# Revit family: RN 90033 Optifitt-Serra-Verlängerung
name_source: partatom
category: Rohrformteile
units: mm (PartAtom-declared; Revit-internal decimal feet)

## family parameters
Arbeitsebenenbasiert = Nein
Beim Laden mit Abzugskörper schneiden = Nein
Bemaßung runder Anschluss = Durchmesser verwenden
Gemeinsam genutzt = Nein
Immer vertikal = Ja
Teiletyp = Nicht definiert

## types (15) — shared parameters
1.010.00.2 Blattnummer der Richtlinie = 29
1.010.00.3 Ausgabedatum (Monat) der Richtlinie = 201308
1.010.00.4 Herstellername = R. Nussbaum AG
1.010.00.5 Revisionsdatum der Datei = 20190521
1.010.00.6 Webadresse des Herstellers = http://www.nussbaum.ch
1.100.00.4 Produktbezeichnung = Versorgung
1.110.00.2 Index = 3
1.110.00.4 Produktbezeichnung = Optifitt-Serra
1.960/3L.00.8 Link (URL) = https://www.nussbaum.ch
29.700.00.4 Produktname = Optifitt-Serra-Verlängerung
29.700.00.5 Produktkennung = 2
29.700.00.6 Querschnittsform = 1
29.700.00.7 Nennweitensystem = DN
29.700.00.8 Nenndrucksystem = PN
29.710.02.4 Nenndruck = 16
29.710.02.5 max. zul. Überdruck [hPa] = 1600
29.710.02.7 max. zul. Dauer-Betriebsdruck [hPa] = 1600
29.710.02.9 max. zul. Dauer-Betriebstemperatur [°C] = 90
Connector Visibility = Nein
EnclosingSpace Visibility = Nein
R. Nussbaum AG 90033.18 de Visibility = Nein
R. Nussbaum AG 90033.19 de Visibility = Nein
R. Nussbaum AG 90033.23 de Visibility = Nein
R. Nussbaum AG 90033.24 de Visibility = Nein
R. Nussbaum AG 90033.26 de Visibility = Nein
R. Nussbaum AG 90033.27 de Visibility = Nein
R. Nussbaum AG 90033.28 de Visibility = Nein
R. Nussbaum AG 90033.29 de Visibility = Nein
R. Nussbaum AG 90033.35 de Visibility = Nein
R. Nussbaum AG 90033.36 de Visibility = Nein
R. Nussbaum AG 90033.37 de Visibility = Nein
R. Nussbaum AG 90033.40 de Visibility = Nein
R. Nussbaum AG 90033.41 de Visibility = Nein
R. Nussbaum AG 90033.42 de Visibility = Nein

## per-type parameters (varying)
- DN=25: 1.800.00.3 TGA-Nummer=01900300000000000000000000000000000000000000000020000000000000000048; 1.800.00.4 Kommentarfeld=90033.50, Optifitt-Serra-Verlängerung, DN=25, L=25, R=1, Rp=1; 1.810.00.3 Hersteller-Bestellnummer=90033.50; 1.810.00.4 DATANORM-Nummer=90033.50; 1.810.00.6 GTIN-Nummer=7612945034908; 29.710.02.10 Formstück-Gewicht [kg]=0.147; 29.710.02.3 Benennung=Optifitt-Serra-Verlängerung, DN=25, L=25, R=1, Rp=1; CONNECTOR0_DIAMETER_dX_0r=25 mm  [stored 0.082021 ft]; CONNECTOR0_dX_01=17 mm  [stored 0.0557743 ft]; CONNECTOR0_ref_dX=17 mm  [stored 0.0557743 ft]; CONNECTOR1_DIAMETER_dX_0r=25 mm  [stored 0.082021 ft]; CONNECTOR1_dX_00=28 mm; CONNECTOR1_dX_01=45 mm; CONNECTOR1_ref_dX=28 mm; CONNECTOR1_ref_dX2=45 mm; R. Nussbaum AG 90033.14 de Visibility=Nein; R. Nussbaum AG 90033.15 de Visibility=Nein; R. Nussbaum AG 90033.16 de Visibility=Nein; R. Nussbaum AG 90033.17 de Visibility=Nein; R. Nussbaum AG 90033.22 de Visibility=Nein; R. Nussbaum AG 90033.30 de Visibility=Nein; R. Nussbaum AG 90033.34 de Visibility=Nein; R. Nussbaum AG 90033.45 de Visibility=Nein; R. Nussbaum AG 90033.46 de Visibility=Nein; R. Nussbaum AG 90033.47 de Visibility=Nein; R. Nussbaum AG 90033.48 de Visibility=Nein; R. Nussbaum AG 90033.50 de Visibility=Ja; R. Nussbaum AG 90033.51 de Visibility=Nein; R. Nussbaum AG 90033.52 de Visibility=Nein; R. Nussbaum AG 90033.53 de Visibility=Nein
- DN=15: 1.800.00.3 TGA-Nummer=01900300000000000000000000000000000000000000000020000000000000000007; 1.800.00.4 Kommentarfeld=90033.22, Optifitt-Serra-Verlängerung, DN=15, L=12.5, R=½, Rp=½; 1.810.00.3 Hersteller-Bestellnummer=90033.22; 1.810.00.4 DATANORM-Nummer=90033.22; 1.810.00.6 GTIN-Nummer=7612945714909; 29.710.02.10 Formstück-Gewicht [kg]=0.052; 29.710.02.3 Benennung=Optifitt-Serra-Verlängerung, DN=15, L=12.5, R=½, Rp=½; CONNECTOR0_DIAMETER_dX_0r=15 mm; CONNECTOR0_dX_01=13 mm; CONNECTOR0_ref_dX=13 mm; CONNECTOR1_DIAMETER_dX_0r=15 mm; CONNECTOR1_dX_00=15 mm; CONNECTOR1_dX_01=28 mm; CONNECTOR1_ref_dX=15 mm; CONNECTOR1_ref_dX2=28 mm; R. Nussbaum AG 90033.14 de Visibility=Nein; R. Nussbaum AG 90033.15 de Visibility=Nein; R. Nussbaum AG 90033.16 de Visibility=Nein; R. Nussbaum AG 90033.17 de Visibility=Nein; R. Nussbaum AG 90033.22 de Visibility=Ja; R. Nussbaum AG 90033.30 de Visibility=Nein; R. Nussbaum AG 90033.34 de Visibility=Nein; R. Nussbaum AG 90033.45 de Visibility=Nein; R. Nussbaum AG 90033.46 de Visibility=Nein; R. Nussbaum AG 90033.47 de Visibility=Nein; R. Nussbaum AG 90033.48 de Visibility=Nein; R. Nussbaum AG 90033.50 de Visibility=Nein; R. Nussbaum AG 90033.51 de Visibility=Nein; R. Nussbaum AG 90033.52 de Visibility=Nein; R. Nussbaum AG 90033.53 de Visibility=Nein
- DN=2: 1.800.00.3 TGA-Nummer=01900300000000000000000000000000000000000000000020000000000000000046; 1.800.00.4 Kommentarfeld=90033.30, Optifitt-Serra-Verlängerung, DN=15, L=50, R=½, Rp=½; 1.810.00.3 Hersteller-Bestellnummer=90033.3; 1.810.00.4 DATANORM-Nummer=90033.3; 1.810.00.6 GTIN-Nummer=7612945034786; 29.710.02.10 Formstück-Gewicht [kg]=0.143; 29.710.02.3 Benennung=Optifitt-Serra-Verlängerung, DN=15, L=50, R=½, Rp=½; CONNECTOR0_DIAMETER_dX_0r=15 mm; CONNECTOR0_dX_01=13 mm; CONNECTOR0_ref_dX=13 mm; CONNECTOR1_DIAMETER_dX_0r=15 mm; CONNECTOR1_dX_00=53 mm; CONNECTOR1_dX_01=66 mm; CONNECTOR1_ref_dX=53 mm; CONNECTOR1_ref_dX2=66 mm; Hersteller=R. Nussbaum AG; Modell=90033.3; R. Nussbaum AG 90033.14 de Visibility=Nein; R. Nussbaum AG 90033.15 de Visibility=Nein; R. Nussbaum AG 90033.16 de Visibility=Nein; R. Nussbaum AG 90033.17 de Visibility=Nein; R. Nussbaum AG 90033.22 de Visibility=Nein; R. Nussbaum AG 90033.30 de Visibility=Ja; R. Nussbaum AG 90033.34 de Visibility=Nein; R. Nussbaum AG 90033.45 de Visibility=Nein; R. Nussbaum AG 90033.46 de Visibility=Nein; R. Nussbaum AG 90033.47 de Visibility=Nein; R. Nussbaum AG 90033.48 de Visibility=Nein; R. Nussbaum AG 90033.50 de Visibility=Nein; R. Nussbaum AG 90033.51 de Visibility=Nein; R. Nussbaum AG 90033.52 de Visibility=Nein; R. Nussbaum AG 90033.53 de Visibility=Nein; Typenkommentare=Optifitt-Serra-Verlängerung  DN=15; URL=https://www.nussbaum.ch
- DN=1: 1.800.00.3 TGA-Nummer=01900300000000000000000000000000000000000000000020000000000000000026; 1.800.00.4 Kommentarfeld=90033.53, Optifitt-Serra-Verlängerung, DN=25, L=50, R=1, Rp=1; 1.810.00.3 Hersteller-Bestellnummer=90033.53; 1.810.00.4 DATANORM-Nummer=90033.53; 1.810.00.6 GTIN-Nummer=7612945034939; 29.710.02.10 Formstück-Gewicht [kg]=0.239; 29.710.02.3 Benennung=Optifitt-Serra-Verlängerung, DN=25, L=50, R=1, Rp=1; CONNECTOR0_DIAMETER_dX_0r=25 mm  [stored 0.082021 ft]; CONNECTOR0_dX_01=17 mm  [stored 0.0557743 ft]; CONNECTOR0_ref_dX=17 mm  [stored 0.0557743 ft]; CONNECTOR1_DIAMETER_dX_0r=25 mm  [stored 0.082021 ft]; CONNECTOR1_dX_00=53 mm; CONNECTOR1_dX_01=70 mm; CONNECTOR1_ref_dX=53 mm; CONNECTOR1_ref_dX2=70 mm; Hersteller=R. Nussbaum AG; Modell=90033.53; R. Nussbaum AG 90033.14 de Visibility=Nein; R. Nussbaum AG 90033.15 de Visibility=Nein; R. Nussbaum AG 90033.16 de Visibility=Nein; R. Nussbaum AG 90033.17 de Visibility=Nein; R. Nussbaum AG 90033.22 de Visibility=Nein; R. Nussbaum AG 90033.30 de Visibility=Nein; R. Nussbaum AG 90033.34 de Visibility=Nein; R. Nussbaum AG 90033.45 de Visibility=Nein; R. Nussbaum AG 90033.46 de Visibility=Nein; R. Nussbaum AG 90033.47 de Visibility=Nein; R. Nussbaum AG 90033.48 de Visibility=Nein; R. Nussbaum AG 90033.50 de Visibility=Nein; R. Nussbaum AG 90033.51 de Visibility=Nein; R. Nussbaum AG 90033.52 de Visibility=Nein; R. Nussbaum AG 90033.53 de Visibility=Ja; Typenkommentare=Optifitt-Serra-Verlängerung  DN=25; URL=https://www.nussbaum.ch
- DN=3: 1.800.00.3 TGA-Nummer=01900300000000000000000000000000000000000000000020000000000000000025; 1.800.00.4 Kommentarfeld=90033.52, Optifitt-Serra-Verlängerung, DN=25, L=40, R=1, Rp=1; 1.810.00.3 Hersteller-Bestellnummer=90033.52; 1.810.00.4 DATANORM-Nummer=90033.52; 1.810.00.5 StLB-Nummer=214.414; 1.810.00.6 GTIN-Nummer=7612945034922; 29.710.02.10 Formstück-Gewicht [kg]=0.2; 29.710.02.3 Benennung=Optifitt-Serra-Verlängerung, DN=25, L=40, R=1, Rp=1; CONNECTOR0_DIAMETER_dX_0r=25 mm  [stored 0.082021 ft]; CONNECTOR0_dX_01=17 mm  [stored 0.0557743 ft]; CONNECTOR0_ref_dX=17 mm  [stored 0.0557743 ft]; CONNECTOR1_DIAMETER_dX_0r=25 mm  [stored 0.082021 ft]; CONNECTOR1_dX_00=43 mm; CONNECTOR1_dX_01=60 mm  [stored 0.19685 ft]; CONNECTOR1_ref_dX=43 mm; CONNECTOR1_ref_dX2=60 mm  [stored 0.19685 ft]; Hersteller=R. Nussbaum AG; Modell=90033.52; R. Nussbaum AG 90033.14 de Visibility=Nein; R. Nussbaum AG 90033.15 de Visibility=Nein; R. Nussbaum AG 90033.16 de Visibility=Nein; R. Nussbaum AG 90033.17 de Visibility=Nein; R. Nussbaum AG 90033.22 de Visibility=Nein; R. Nussbaum AG 90033.30 de Visibility=Nein; R. Nussbaum AG 90033.34 de Visibility=Nein; R. Nussbaum AG 90033.45 de Visibility=Nein; R. Nussbaum AG 90033.46 de Visibility=Nein; R. Nussbaum AG 90033.47 de Visibility=Nein; R. Nussbaum AG 90033.48 de Visibility=Nein; R. Nussbaum AG 90033.50 de Visibility=Nein; R. Nussbaum AG 90033.51 de Visibility=Nein; R. Nussbaum AG 90033.52 de Visibility=Ja; R. Nussbaum AG 90033.53 de Visibility=Nein; Typenkommentare=Optifitt-Serra-Verlängerung  DN=25; URL=https://www.nussbaum.ch
- DN=4: 1.800.00.3 TGA-Nummer=01900300000000000000000000000000000000000000000020000000000000000024; 1.800.00.4 Kommentarfeld=90033.51, Optifitt-Serra-Verlängerung, DN=25, L=30, R=1, Rp=1; 1.810.00.3 Hersteller-Bestellnummer=90033.51; 1.810.00.4 DATANORM-Nummer=90033.51; 1.810.00.6 GTIN-Nummer=7612945034915; 29.710.02.10 Formstück-Gewicht [kg]=0.171; 29.710.02.3 Benennung=Optifitt-Serra-Verlängerung, DN=25, L=30, R=1, Rp=1; CONNECTOR0_DIAMETER_dX_0r=25 mm  [stored 0.082021 ft]; CONNECTOR0_dX_01=17 mm  [stored 0.0557743 ft]; CONNECTOR0_ref_dX=17 mm  [stored 0.0557743 ft]; CONNECTOR1_DIAMETER_dX_0r=25 mm  [stored 0.082021 ft]; CONNECTOR1_dX_00=33 mm; CONNECTOR1_dX_01=50 mm; CONNECTOR1_ref_dX=33 mm; CONNECTOR1_ref_dX2=50 mm; Hersteller=R. Nussbaum AG; Modell=90033.51; R. Nussbaum AG 90033.14 de Visibility=Nein; R. Nussbaum AG 90033.15 de Visibility=Nein; R. Nussbaum AG 90033.16 de Visibility=Nein; R. Nussbaum AG 90033.17 de Visibility=Nein; R. Nussbaum AG 90033.22 de Visibility=Nein; R. Nussbaum AG 90033.30 de Visibility=Nein; R. Nussbaum AG 90033.34 de Visibility=Nein; R. Nussbaum AG 90033.45 de Visibility=Nein; R. Nussbaum AG 90033.46 de Visibility=Nein; R. Nussbaum AG 90033.47 de Visibility=Nein; R. Nussbaum AG 90033.48 de Visibility=Nein; R. Nussbaum AG 90033.50 de Visibility=Nein; R. Nussbaum AG 90033.51 de Visibility=Ja; R. Nussbaum AG 90033.52 de Visibility=Nein; R. Nussbaum AG 90033.53 de Visibility=Nein; Typenkommentare=Optifitt-Serra-Verlängerung  DN=25; URL=https://www.nussbaum.ch
- DN=6: 1.800.00.3 TGA-Nummer=01900300000000000000000000000000000000000000000020000000000000000023; 1.800.00.4 Kommentarfeld=90033.48, Optifitt-Serra-Verlängerung, DN=20, L=100, R=¾, Rp=¾; 1.810.00.3 Hersteller-Bestellnummer=90033.48; 1.810.00.4 DATANORM-Nummer=90033.48; 1.810.00.6 GTIN-Nummer=7612945034892; 29.710.02.10 Formstück-Gewicht [kg]=0.317; 29.710.02.3 Benennung=Optifitt-Serra-Verlängerung, DN=20, L=100, R=¾, Rp=¾; CONNECTOR0_DIAMETER_dX_0r=20 mm; CONNECTOR0_dX_01=15 mm; CONNECTOR0_ref_dX=15 mm; CONNECTOR1_DIAMETER_dX_0r=20 mm; CONNECTOR1_dX_00=102 mm; CONNECTOR1_dX_01=117 mm; CONNECTOR1_ref_dX=102 mm; CONNECTOR1_ref_dX2=117 mm; Hersteller=R. Nussbaum AG; Modell=90033.48; R. Nussbaum AG 90033.14 de Visibility=Nein; R. Nussbaum AG 90033.15 de Visibility=Nein; R. Nussbaum AG 90033.16 de Visibility=Nein; R. Nussbaum AG 90033.17 de Visibility=Nein; R. Nussbaum AG 90033.22 de Visibility=Nein; R. Nussbaum AG 90033.30 de Visibility=Nein; R. Nussbaum AG 90033.34 de Visibility=Nein; R. Nussbaum AG 90033.45 de Visibility=Nein; R. Nussbaum AG 90033.46 de Visibility=Nein; R. Nussbaum AG 90033.47 de Visibility=Nein; R. Nussbaum AG 90033.48 de Visibility=Ja; R. Nussbaum AG 90033.50 de Visibility=Nein; R. Nussbaum AG 90033.51 de Visibility=Nein; R. Nussbaum AG 90033.52 de Visibility=Nein; R. Nussbaum AG 90033.53 de Visibility=Nein; Typenkommentare=Optifitt-Serra-Verlängerung  DN=20; URL=https://www.nussbaum.ch
- DN=5: 1.800.00.3 TGA-Nummer=01900300000000000000000000000000000000000000000020000000000000000022; 1.800.00.4 Kommentarfeld=90033.47, Optifitt-Serra-Verlängerung, DN=20, L=80, R=¾, Rp=¾; 1.810.00.3 Hersteller-Bestellnummer=90033.47; 1.810.00.4 DATANORM-Nummer=90033.47; 1.810.00.6 GTIN-Nummer=7612945034885; 29.710.02.10 Formstück-Gewicht [kg]=0.256; 29.710.02.3 Benennung=Optifitt-Serra-Verlängerung, DN=20, L=80, R=¾, Rp=¾; CONNECTOR0_DIAMETER_dX_0r=20 mm; CONNECTOR0_dX_01=15 mm; CONNECTOR0_ref_dX=15 mm; CONNECTOR1_DIAMETER_dX_0r=20 mm; CONNECTOR1_dX_00=82 mm; CONNECTOR1_dX_01=97 mm; CONNECTOR1_ref_dX=82 mm; CONNECTOR1_ref_dX2=97 mm; Hersteller=R. Nussbaum AG; Modell=90033.47; R. Nussbaum AG 90033.14 de Visibility=Nein; R. Nussbaum AG 90033.15 de Visibility=Nein; R. Nussbaum AG 90033.16 de Visibility=Nein; R. Nussbaum AG 90033.17 de Visibility=Nein; R. Nussbaum AG 90033.22 de Visibility=Nein; R. Nussbaum AG 90033.30 de Visibility=Nein; R. Nussbaum AG 90033.34 de Visibility=Nein; R. Nussbaum AG 90033.45 de Visibility=Nein; R. Nussbaum AG 90033.46 de Visibility=Nein; R. Nussbaum AG 90033.47 de Visibility=Ja; R. Nussbaum AG 90033.48 de Visibility=Nein; R. Nussbaum AG 90033.50 de Visibility=Nein; R. Nussbaum AG 90033.51 de Visibility=Nein; R. Nussbaum AG 90033.52 de Visibility=Nein; R. Nussbaum AG 90033.53 de Visibility=Nein; Typenkommentare=Optifitt-Serra-Verlängerung  DN=20; URL=https://www.nussbaum.ch
- DN=8: 1.800.00.3 TGA-Nummer=01900300000000000000000000000000000000000000000020000000000000000021; 1.800.00.4 Kommentarfeld=90033.46, Optifitt-Serra-Verlängerung, DN=20, L=65, R=¾, Rp=¾; 1.810.00.3 Hersteller-Bestellnummer=90033.46; 1.810.00.4 DATANORM-Nummer=90033.46; 1.810.00.6 GTIN-Nummer=7612945034878; 29.710.02.10 Formstück-Gewicht [kg]=0.206; 29.710.02.3 Benennung=Optifitt-Serra-Verlängerung, DN=20, L=65, R=¾, Rp=¾; CONNECTOR0_DIAMETER_dX_0r=20 mm; CONNECTOR0_dX_01=15 mm; CONNECTOR0_ref_dX=15 mm; CONNECTOR1_DIAMETER_dX_0r=20 mm; CONNECTOR1_dX_00=67 mm; CONNECTOR1_dX_01=82 mm; CONNECTOR1_ref_dX=67 mm; CONNECTOR1_ref_dX2=82 mm; Hersteller=R. Nussbaum AG; Modell=90033.46; R. Nussbaum AG 90033.14 de Visibility=Nein; R. Nussbaum AG 90033.15 de Visibility=Nein; R. Nussbaum AG 90033.16 de Visibility=Nein; R. Nussbaum AG 90033.17 de Visibility=Nein; R. Nussbaum AG 90033.22 de Visibility=Nein; R. Nussbaum AG 90033.30 de Visibility=Nein; R. Nussbaum AG 90033.34 de Visibility=Nein; R. Nussbaum AG 90033.45 de Visibility=Nein; R. Nussbaum AG 90033.46 de Visibility=Ja; R. Nussbaum AG 90033.47 de Visibility=Nein; R. Nussbaum AG 90033.48 de Visibility=Nein; R. Nussbaum AG 90033.50 de Visibility=Nein; R. Nussbaum AG 90033.51 de Visibility=Nein; R. Nussbaum AG 90033.52 de Visibility=Nein; R. Nussbaum AG 90033.53 de Visibility=Nein; Typenkommentare=Optifitt-Serra-Verlängerung  DN=20; URL=https://www.nussbaum.ch
- DN=7: 1.800.00.3 TGA-Nummer=01900300000000000000000000000000000000000000000020000000000000000020; 1.800.00.4 Kommentarfeld=90033.45, Optifitt-Serra-Verlängerung, DN=20, L=25, R=¾, Rp=¾; 1.810.00.3 Hersteller-Bestellnummer=90033.45; 1.810.00.4 DATANORM-Nummer=90033.45; 1.810.00.6 GTIN-Nummer=7612945034861; 29.710.02.10 Formstück-Gewicht [kg]=0.106; 29.710.02.3 Benennung=Optifitt-Serra-Verlängerung, DN=20, L=25, R=¾, Rp=¾; CONNECTOR0_DIAMETER_dX_0r=20 mm; CONNECTOR0_dX_01=15 mm; CONNECTOR0_ref_dX=15 mm; CONNECTOR1_DIAMETER_dX_0r=20 mm; CONNECTOR1_dX_00=27 mm; CONNECTOR1_dX_01=42 mm; CONNECTOR1_ref_dX=27 mm; CONNECTOR1_ref_dX2=42 mm; Hersteller=R. Nussbaum AG; Modell=90033.45; R. Nussbaum AG 90033.14 de Visibility=Nein; R. Nussbaum AG 90033.15 de Visibility=Nein; R. Nussbaum AG 90033.16 de Visibility=Nein; R. Nussbaum AG 90033.17 de Visibility=Nein; R. Nussbaum AG 90033.22 de Visibility=Nein; R. Nussbaum AG 90033.30 de Visibility=Nein; R. Nussbaum AG 90033.34 de Visibility=Nein; R. Nussbaum AG 90033.45 de Visibility=Ja; R. Nussbaum AG 90033.46 de Visibility=Nein; R. Nussbaum AG 90033.47 de Visibility=Nein; R. Nussbaum AG 90033.48 de Visibility=Nein; R. Nussbaum AG 90033.50 de Visibility=Nein; R. Nussbaum AG 90033.51 de Visibility=Nein; R. Nussbaum AG 90033.52 de Visibility=Nein; R. Nussbaum AG 90033.53 de Visibility=Nein; Typenkommentare=Optifitt-Serra-Verlängerung  DN=20; URL=https://www.nussbaum.ch
- DN=20: 1.800.00.3 TGA-Nummer=01900300000000000000000000000000000000000000000020000000000000000014; 1.800.00.4 Kommentarfeld=90033.34, Optifitt-Serra-Verlängerung, DN=20, L=20, R=¾, Rp=¾; 1.810.00.3 Hersteller-Bestellnummer=90033.34; 1.810.00.4 DATANORM-Nummer=90033.34; 1.810.00.6 GTIN-Nummer=7612945034793; 29.710.02.10 Formstück-Gewicht [kg]=0.09; 29.710.02.3 Benennung=Optifitt-Serra-Verlängerung, DN=20, L=20, R=¾, Rp=¾; CONNECTOR0_DIAMETER_dX_0r=20 mm; CONNECTOR0_dX_01=15 mm; CONNECTOR0_ref_dX=15 mm; CONNECTOR1_DIAMETER_dX_0r=20 mm; CONNECTOR1_dX_00=22 mm; CONNECTOR1_dX_01=37 mm; CONNECTOR1_ref_dX=22 mm; CONNECTOR1_ref_dX2=37 mm; R. Nussbaum AG 90033.14 de Visibility=Nein; R. Nussbaum AG 90033.15 de Visibility=Nein; R. Nussbaum AG 90033.16 de Visibility=Nein; R. Nussbaum AG 90033.17 de Visibility=Nein; R. Nussbaum AG 90033.22 de Visibility=Nein; R. Nussbaum AG 90033.30 de Visibility=Nein; R. Nussbaum AG 90033.34 de Visibility=Ja; R. Nussbaum AG 90033.45 de Visibility=Nein; R. Nussbaum AG 90033.46 de Visibility=Nein; R. Nussbaum AG 90033.47 de Visibility=Nein; R. Nussbaum AG 90033.48 de Visibility=Nein; R. Nussbaum AG 90033.50 de Visibility=Nein; R. Nussbaum AG 90033.51 de Visibility=Nein; R. Nussbaum AG 90033.52 de Visibility=Nein; R. Nussbaum AG 90033.53 de Visibility=Nein
- DN=10: 1.800.00.3 TGA-Nummer=01900300000000000000000000000000000000000000000020000000000000000004; 1.800.00.4 Kommentarfeld=90033.17, Optifitt-Serra-Verlängerung, DN=10, L=30, R=3/8, Rp=3/8; 1.810.00.3 Hersteller-Bestellnummer=90033.17; 1.810.00.4 DATANORM-Nummer=90033.17; 1.810.00.6 GTIN-Nummer=7612945034700; 29.710.02.10 Formstück-Gewicht [kg]=0.062; 29.710.02.3 Benennung=Optifitt-Serra-Verlängerung, DN=10, L=30, R=3/8, Rp=3/8; CONNECTOR0_DIAMETER_dX_0r=10 mm  [stored 0.0328084 ft]; CONNECTOR0_dX_01=10 mm  [stored 0.0328084 ft]; CONNECTOR0_ref_dX=10 mm  [stored 0.0328084 ft]; CONNECTOR1_DIAMETER_dX_0r=10 mm  [stored 0.0328084 ft]; CONNECTOR1_dX_00=32 mm; CONNECTOR1_dX_01=42 mm; CONNECTOR1_ref_dX=32 mm; CONNECTOR1_ref_dX2=42 mm; R. Nussbaum AG 90033.14 de Visibility=Nein; R. Nussbaum AG 90033.15 de Visibility=Nein; R. Nussbaum AG 90033.16 de Visibility=Nein; R. Nussbaum AG 90033.17 de Visibility=Ja; R. Nussbaum AG 90033.22 de Visibility=Nein; R. Nussbaum AG 90033.30 de Visibility=Nein; R. Nussbaum AG 90033.34 de Visibility=Nein; R. Nussbaum AG 90033.45 de Visibility=Nein; R. Nussbaum AG 90033.46 de Visibility=Nein; R. Nussbaum AG 90033.47 de Visibility=Nein; R. Nussbaum AG 90033.48 de Visibility=Nein; R. Nussbaum AG 90033.50 de Visibility=Nein; R. Nussbaum AG 90033.51 de Visibility=Nein; R. Nussbaum AG 90033.52 de Visibility=Nein; R. Nussbaum AG 90033.53 de Visibility=Nein
- DN=11: 1.800.00.3 TGA-Nummer=01900300000000000000000000000000000000000000000020000000000000000003; 1.800.00.4 Kommentarfeld=90033.16, Optifitt-Serra-Verlängerung, DN=10, L=25, R=3/8, Rp=3/8; 1.810.00.3 Hersteller-Bestellnummer=90033.16; 1.810.00.4 DATANORM-Nummer=90033.16; 1.810.00.6 GTIN-Nummer=7612945034694; 29.710.02.10 Formstück-Gewicht [kg]=0.051; 29.710.02.3 Benennung=Optifitt-Serra-Verlängerung, DN=10, L=25, R=3/8, Rp=3/8; CONNECTOR0_DIAMETER_dX_0r=10 mm  [stored 0.0328084 ft]; CONNECTOR0_dX_01=10 mm  [stored 0.0328084 ft]; CONNECTOR0_ref_dX=10 mm  [stored 0.0328084 ft]; CONNECTOR1_DIAMETER_dX_0r=10 mm  [stored 0.0328084 ft]; CONNECTOR1_dX_00=27 mm; CONNECTOR1_dX_01=37 mm; CONNECTOR1_ref_dX=27 mm; CONNECTOR1_ref_dX2=37 mm; Hersteller=R. Nussbaum AG; Modell=90033.16; R. Nussbaum AG 90033.14 de Visibility=Nein; R. Nussbaum AG 90033.15 de Visibility=Nein; R. Nussbaum AG 90033.16 de Visibility=Ja; R. Nussbaum AG 90033.17 de Visibility=Nein; R. Nussbaum AG 90033.22 de Visibility=Nein; R. Nussbaum AG 90033.30 de Visibility=Nein; R. Nussbaum AG 90033.34 de Visibility=Nein; R. Nussbaum AG 90033.45 de Visibility=Nein; R. Nussbaum AG 90033.46 de Visibility=Nein; R. Nussbaum AG 90033.47 de Visibility=Nein; R. Nussbaum AG 90033.48 de Visibility=Nein; R. Nussbaum AG 90033.50 de Visibility=Nein; R. Nussbaum AG 90033.51 de Visibility=Nein; R. Nussbaum AG 90033.52 de Visibility=Nein; R. Nussbaum AG 90033.53 de Visibility=Nein; Typenkommentare=Optifitt-Serra-Verlängerung  DN=10; URL=https://www.nussbaum.ch
- DN=9: 1.800.00.3 TGA-Nummer=01900300000000000000000000000000000000000000000020000000000000000002; 1.800.00.4 Kommentarfeld=90033.15, Optifitt-Serra-Verlängerung, DN=10, L=20, R=3/8, Rp=3/8; 1.810.00.3 Hersteller-Bestellnummer=90033.15; 1.810.00.4 DATANORM-Nummer=90033.15; 1.810.00.6 GTIN-Nummer=7612945034687; 29.710.02.10 Formstück-Gewicht [kg]=0.043; 29.710.02.3 Benennung=Optifitt-Serra-Verlängerung, DN=10, L=20, R=3/8, Rp=3/8; CONNECTOR0_DIAMETER_dX_0r=10 mm  [stored 0.0328084 ft]; CONNECTOR0_dX_01=10 mm  [stored 0.0328084 ft]; CONNECTOR0_ref_dX=10 mm  [stored 0.0328084 ft]; CONNECTOR1_DIAMETER_dX_0r=10 mm  [stored 0.0328084 ft]; CONNECTOR1_dX_00=22 mm; CONNECTOR1_dX_01=32 mm; CONNECTOR1_ref_dX=22 mm; CONNECTOR1_ref_dX2=32 mm; Hersteller=R. Nussbaum AG; Modell=90033.15; R. Nussbaum AG 90033.14 de Visibility=Nein; R. Nussbaum AG 90033.15 de Visibility=Ja; R. Nussbaum AG 90033.16 de Visibility=Nein; R. Nussbaum AG 90033.17 de Visibility=Nein; R. Nussbaum AG 90033.22 de Visibility=Nein; R. Nussbaum AG 90033.30 de Visibility=Nein; R. Nussbaum AG 90033.34 de Visibility=Nein; R. Nussbaum AG 90033.45 de Visibility=Nein; R. Nussbaum AG 90033.46 de Visibility=Nein; R. Nussbaum AG 90033.47 de Visibility=Nein; R. Nussbaum AG 90033.48 de Visibility=Nein; R. Nussbaum AG 90033.50 de Visibility=Nein; R. Nussbaum AG 90033.51 de Visibility=Nein; R. Nussbaum AG 90033.52 de Visibility=Nein; R. Nussbaum AG 90033.53 de Visibility=Nein; Typenkommentare=Optifitt-Serra-Verlängerung  DN=10; URL=https://www.nussbaum.ch
- DN=12: 1.800.00.3 TGA-Nummer=01900300000000000000000000000000000000000000000020000000000000000001; 1.800.00.4 Kommentarfeld=90033.14, Optifitt-Serra-Verlängerung, DN=10, L=15, R=3/8, Rp=3/8; 1.810.00.3 Hersteller-Bestellnummer=90033.14; 1.810.00.4 DATANORM-Nummer=90033.14; 1.810.00.6 GTIN-Nummer=7612945034670; 29.710.02.10 Formstück-Gewicht [kg]=0.035; 29.710.02.3 Benennung=Optifitt-Serra-Verlängerung, DN=10, L=15, R=3/8, Rp=3/8; CONNECTOR0_DIAMETER_dX_0r=10 mm  [stored 0.0328084 ft]; CONNECTOR0_dX_01=10 mm  [stored 0.0328084 ft]; CONNECTOR0_ref_dX=10 mm  [stored 0.0328084 ft]; CONNECTOR1_DIAMETER_dX_0r=10 mm  [stored 0.0328084 ft]; CONNECTOR1_dX_00=17 mm  [stored 0.0557743 ft]; CONNECTOR1_dX_01=27 mm; CONNECTOR1_ref_dX=17 mm  [stored 0.0557743 ft]; CONNECTOR1_ref_dX2=27 mm; Hersteller=R. Nussbaum AG; Modell=90033.14; R. Nussbaum AG 90033.14 de Visibility=Ja; R. Nussbaum AG 90033.15 de Visibility=Nein; R. Nussbaum AG 90033.16 de Visibility=Nein; R. Nussbaum AG 90033.17 de Visibility=Nein; R. Nussbaum AG 90033.22 de Visibility=Nein; R. Nussbaum AG 90033.30 de Visibility=Nein; R. Nussbaum AG 90033.34 de Visibility=Nein; R. Nussbaum AG 90033.45 de Visibility=Nein; R. Nussbaum AG 90033.46 de Visibility=Nein; R. Nussbaum AG 90033.47 de Visibility=Nein; R. Nussbaum AG 90033.48 de Visibility=Nein; R. Nussbaum AG 90033.50 de Visibility=Nein; R. Nussbaum AG 90033.51 de Visibility=Nein; R. Nussbaum AG 90033.52 de Visibility=Nein; R. Nussbaum AG 90033.53 de Visibility=Nein; Typenkommentare=Optifitt-Serra-Verlängerung  DN=10; URL=https://www.nussbaum.ch

note: [stored X ft] marks values corroborated as IEEE doubles in the binary element streams (Revit-internal decimal feet)

## geometry (parser evidence)
native form markers: Sweep x3
no freeform markers — native parametric forms only
